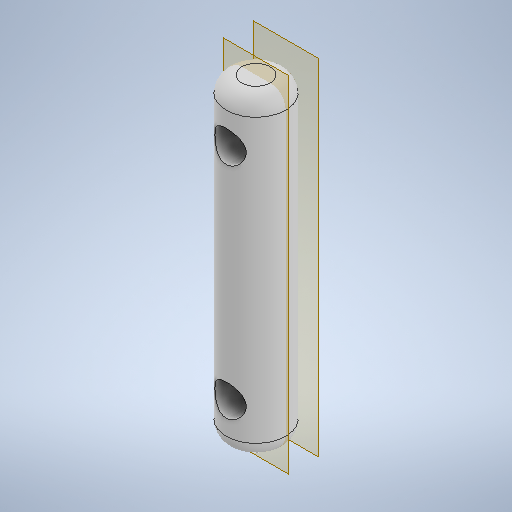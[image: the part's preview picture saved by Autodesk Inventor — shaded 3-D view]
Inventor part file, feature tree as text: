
AUTODESK INVENTOR PART (.ipt)
format: ipt  version: 2025.2 (Build 292293000, 293)  size: 270,336 bytes
history: native  units: mm
features: extrude x2, sketch x2, plane x1, fillet x1
ambient origin geometry x8: Origin, YZ Plane, XZ Plane, XY Plane, X Axis, Y Axis, Z Axis, Center Point
bodies: Solid1 (feature_tree)
feature tree (6):
  extrude  "Extrusion1"  Depth=100.0mm TaperAngle=0.0deg
  plane  "Work Plane1"
  extrude  "Extrusion2"  Depth=5.0mm
  fillet  "Fillet1"  Radius=35.0mm
  sketch  "Sketch1"  dims[d0=19.0mm d1=100.0mm d2=0.0mm]
  sketch  "Sketch2"  dims[d3=-9.5mm d4=35.0mm d5=35.0mm d6=10.0mm d7=10.0mm d8=20.0mm d9=0.0mm d10=5.0mm]
